# Revit family: PRD_FrankeWS_JntrlUnits_SiriusMultiPurposeSink_BS340
name_source: partatom
category: Plumbing Fixtures
revit_build: Autodesk Revit 2018 (Build: 20190510_1515(x64)
units: mm (PartAtom-declared; Revit-internal decimal feet)

## family parameters
Cut with Voids When Loaded = No
Host = Face
OmniClass Number = 23.45.05.14.14
OmniClass Title = Sinks/Lavatories
Part Type = Normal
Room Calculation Point = No
Round Connector Dimension = Use Diameter
Shared = No

## types (1)
- BS340
    AssetType = Fixed
    BIMObjectName = PRD_AR_JanitorialUnits_SiriusMultiPurposeSink_BS340
    Category = Pr_40_20_96_44, Janitorial sinks
    Color = Stainless steel
    Default Elevation = 0 mm  [stored 0 ft]
    Description = General purpose sink for inset mounting, stainless steel, surface satin finished, material thickness 1 mm, seamless welded bowl with dimensions 500x380x230 mm, 1 1/2'' plug waste with plastic overflow pipe, drainage back centric, incl. washer and clamps for inset mounting. Outcut diameter: 540 x 450 mm
    DrainSize = DN-40-1-1-2INH
    DurationUnit = year
    Features = stainless steel, 1.00 mm, satin finished, inset mounting, 565x230x475 mm (WxHxD)
    Finish = Satin finished
    FinishAndMaterial = Stainless steel 1.4301
    Form = Stainless steel multi purpose sink
    GrossWeight = 5.20 kg
    IfcExportAs = IfcSanitaryTerminalType
    IfcExportType = SINK
    IntegralAccessories = incl. washer and clamps for inset mounting
    Manufacturer = KWC Group AG
    ManufacturerName = KWC Group AG
    ManufacturerURL = www.kwc.com
    Material = Stainless steel
    Model = BS340
    ModelNumber = 2000057989
    ModelReference = BS340
    NBSDescription = Janitorial units
    NBSReference = 45-35-70/401
    Name = Sirius multi purpose sink BS340
    NetWeight = 4.26 kg
    NominalDepth = 475 mm  [stored 1.5584 ft]
    NominalHeight = 230 mm  [stored 0.754593 ft]
    NominalLength = 0 mm  [stored 0 ft]
    NominalWidth = 565 mm  [stored 1.85367 ft]
    ProductInformation = https://pim.kwc.com
    Shape = Rectangular
    SinkMaterial = PRD_AR_StainlessSteel_SatinFinished
    SinkMounting = CounterTop
    SinkType = Other
    Size = 565 x 475 x 230 mm
    URL = www.kwc.com
    Uniclass2015Code = Pr_40_20_96_44
    Uniclass2015Title = Janitorial sinks
    Uniclass2015Version = Products v1.5
    Version = 1
    WarrantyDurationUnit = year
    WasteSize = 1 1/4"
    WaterSupplyOverflowAndWasteHolesOverflow = Stand pipe overflow
    WaterSupplyOverflowAndWasteHolesWaste = Center-Back
    WaterSupplyOverflowAndWasteHolesWaterSupply = No tapholes

note: [stored X ft] marks values corroborated as IEEE doubles in the binary element streams (Revit-internal decimal feet)

## geometry (parser evidence)
native form markers: Sweep x6
no freeform markers — native parametric forms only
